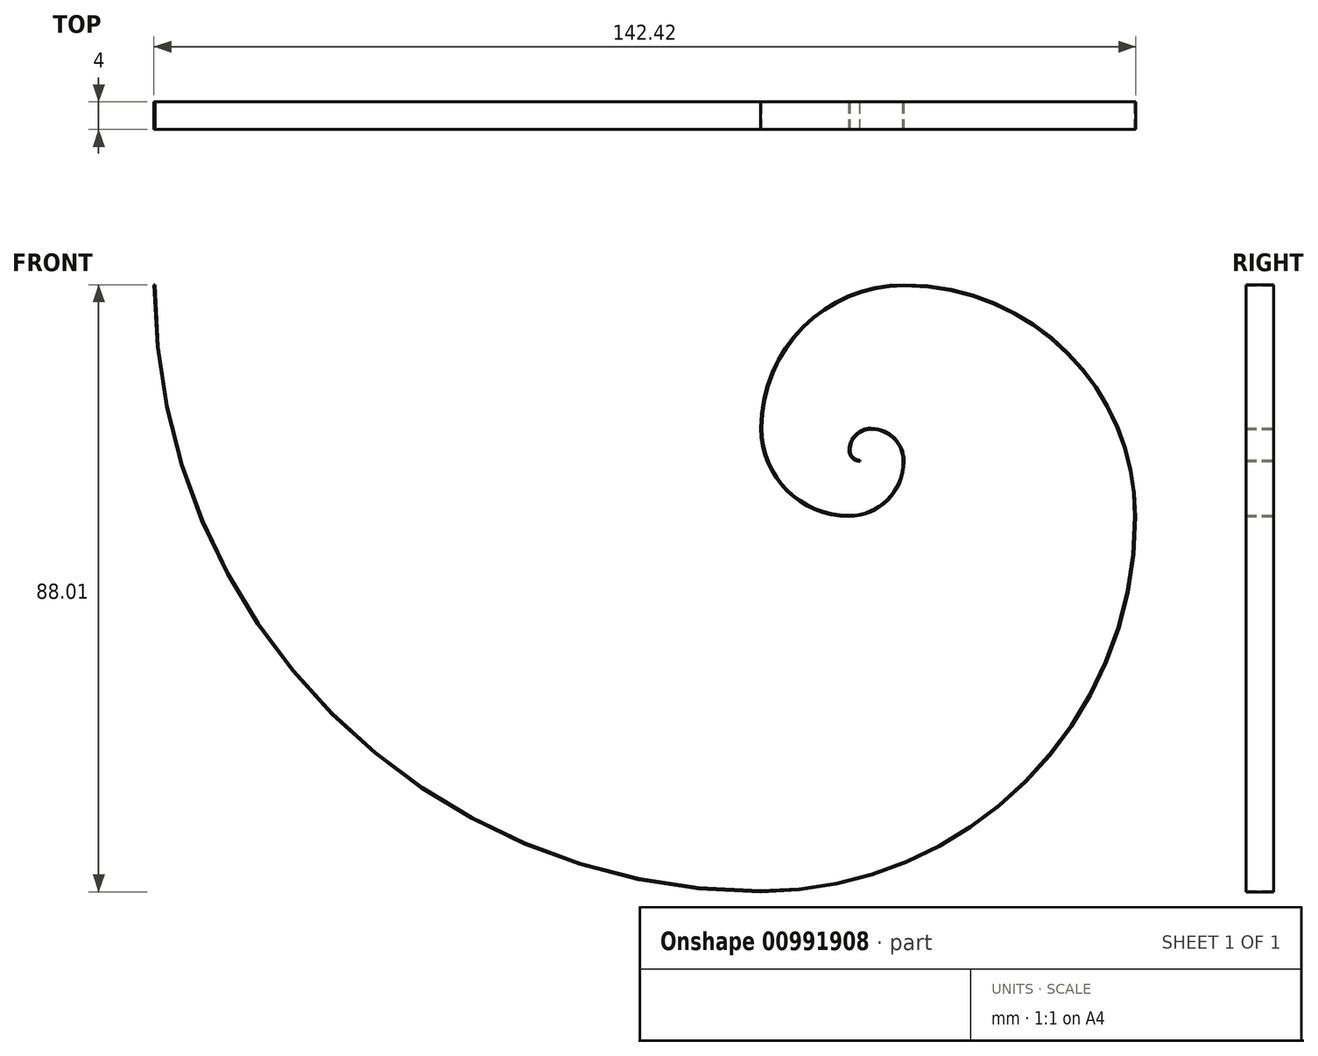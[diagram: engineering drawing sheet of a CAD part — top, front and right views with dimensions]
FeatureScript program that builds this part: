
annotation { "Feature Type Name" : "Feature", "Feature Type Description" : "" }
export const myFeature = defineFeature(function(context is Context, id is Id, definition is map)
    precondition{}
    {
        {
            var Q0;
            Q0=qCreatedBy(makeId("Front.planeOp"),FACE);
            var sketch = newSketch(context, id + "F0", { "sketchPlane" : qUnion([Q0])});
            skLineSegment(sketch, "E0.left", {"start": v(12.7, -12.7) * mm, "end": v(12.7, -10.02) * mm});
            skPoint(sketch, "E0.middle", {"position": v(0, 0) * mm});
            skArc(sketch, "E1", {"start": v(12.7, -12.7) * mm, "mid": v(-5.26, -5.26) * mm, "end": v(-12.7, 12.7) * mm});
            skArc(sketch, "E2", {"start": v(-12.7, 12.7) * mm, "mid": v(2.18, 48.62) * mm, "end": v(38.1, 63.5) * mm});
            skArc(sketch, "E3", {"start": v(38.1, 63.5) * mm, "mid": v(91.98, 41.18) * mm, "end": v(114.3, -12.7) * mm});
            skArc(sketch, "E4", {"start": v(114.3, -12.7) * mm, "mid": v(77.1, -102.5) * mm, "end": v(-12.7, -139.7) * mm});
            skArc(sketch, "E5", {"start": v(-12.7, -139.7) * mm, "mid": v(-156.38, -80.18) * mm, "end": v(-215.9, 63.5) * mm});
            skLineSegment(sketch, "E6.bottom", {"start": v(-1610.22, 393.7) * mm, "end": v(-1612.9, 393.7) * mm});
            skArc(sketch, "E7", {"start": v(-215.9, 63.5) * mm, "mid": v(-119.19, 296.99) * mm, "end": v(114.3, 393.7) * mm});
            skArc(sketch, "E8", {"start": v(114.3, 393.7) * mm, "mid": v(491.47, 237.47) * mm, "end": v(647.7, -139.7) * mm});
            skArc(sketch, "E9", {"start": v(647.7, -139.7) * mm, "mid": v(394.76, -750.36) * mm, "end": v(-215.9, -1003.3) * mm});
            skArc(sketch, "E10", {"start": v(-215.9, -1003.3) * mm, "mid": v(-1203.73, -594.13) * mm, "end": v(-1612.9, 393.7) * mm});
            skArc(sketch, "E11", {"start": v(12.7, -10.02) * mm, "mid": v(-3.37, -3.37) * mm, "end": v(-10.02, 12.7) * mm});
            skArc(sketch, "E12", {"start": v(-10.02, 12.7) * mm, "mid": v(4.07, 46.73) * mm, "end": v(38.1, 60.82) * mm});
            skArc(sketch, "E13", {"start": v(38.1, 60.82) * mm, "mid": v(90.09, 39.29) * mm, "end": v(111.62, -12.7) * mm});
            skArc(sketch, "E14", {"start": v(111.62, -12.7) * mm, "mid": v(75.2, -100.6) * mm, "end": v(-12.7, -137.02) * mm});
            skArc(sketch, "E15", {"start": v(-12.7, -137.02) * mm, "mid": v(-154.5, -78.3) * mm, "end": v(-213.22, 63.5) * mm});
            skArc(sketch, "E16", {"start": v(-213.22, 63.5) * mm, "mid": v(-117.3, 295.1) * mm, "end": v(114.3, 391.02) * mm});
            skArc(sketch, "E17", {"start": v(114.3, 391.02) * mm, "mid": v(489.58, 235.58) * mm, "end": v(645.02, -139.7) * mm});
            skArc(sketch, "E18", {"start": v(645.02, -139.7) * mm, "mid": v(392.86, -748.46) * mm, "end": v(-215.9, -1000.62) * mm});
            skArc(sketch, "E19", {"start": v(-215.9, -1000.62) * mm, "mid": v(-1201.84, -592.24) * mm, "end": v(-1610.22, 393.7) * mm});
            skSolve(sketch);
        }
        {
            var Q0;
            Q0=makeQuery(id+"F0.imprint","IMPRINT",FACE,{"disambiguationData":[TD([[makeQuery(id+"F0.imprint","IMPRINT",EDGE,{"derivedFrom":sQuery(id+"F0.wireOp",EDGE,"E0.left")}),1.0]])]});
            extrude(context, id + "F1", {"entities" : qUnion([Q0]), "depth" : 63.5 * mm, "offsetDistance" : 25.4 * mm});
        }
        {
            var Q0;
            Q0=makeQuery(id+"F1.opExtrude","SWEPT_BODY",BODY,{"disambiguationData":[OSD([sQuery(id+"F0.wireOp",EDGE,"E0.left"),sQuery(id+"F0.wireOp",EDGE,"E1"),sQuery(id+"F0.wireOp",EDGE,"E2"),sQuery(id+"F0.wireOp",EDGE,"E3"),sQuery(id+"F0.wireOp",EDGE,"E4"),sQuery(id+"F0.wireOp",EDGE,"E5"),sQuery(id+"F0.wireOp",EDGE,"E6.bottom"),sQuery(id+"F0.wireOp",EDGE,"E7"),sQuery(id+"F0.wireOp",EDGE,"E8"),sQuery(id+"F0.wireOp",EDGE,"E9"),sQuery(id+"F0.wireOp",EDGE,"E10"),sQuery(id+"F0.wireOp",EDGE,"E11"),sQuery(id+"F0.wireOp",EDGE,"E12"),sQuery(id+"F0.wireOp",EDGE,"E13"),sQuery(id+"F0.wireOp",EDGE,"E14"),sQuery(id+"F0.wireOp",EDGE,"E15"),sQuery(id+"F0.wireOp",EDGE,"E16"),sQuery(id+"F0.wireOp",EDGE,"E17"),sQuery(id+"F0.wireOp",EDGE,"E18"),sQuery(id+"F0.wireOp",EDGE,"E19")])]});
            var Q1;
            Q1=qCreatedBy(makeId("Origin.pointOp"),VERTEX);
            transform(context, id + "F2", {"entities" : qUnion([Q0]), "transformType" : TransformType.SCALE_UNIFORMLY, "scale" : .2, "scalePoint" : qUnion([Q1]), "makeCopy" : false});
        }
        {
            var Q0;
            Q0=makeQuery(id+"F1.opExtrude","SWEPT_BODY",BODY,{"disambiguationData":[OSD([sQuery(id+"F0.wireOp",EDGE,"E0.left"),sQuery(id+"F0.wireOp",EDGE,"E1"),sQuery(id+"F0.wireOp",EDGE,"E2"),sQuery(id+"F0.wireOp",EDGE,"E3"),sQuery(id+"F0.wireOp",EDGE,"E4"),sQuery(id+"F0.wireOp",EDGE,"E5"),sQuery(id+"F0.wireOp",EDGE,"E6.bottom"),sQuery(id+"F0.wireOp",EDGE,"E7"),sQuery(id+"F0.wireOp",EDGE,"E8"),sQuery(id+"F0.wireOp",EDGE,"E9"),sQuery(id+"F0.wireOp",EDGE,"E10"),sQuery(id+"F0.wireOp",EDGE,"E11"),sQuery(id+"F0.wireOp",EDGE,"E12"),sQuery(id+"F0.wireOp",EDGE,"E13"),sQuery(id+"F0.wireOp",EDGE,"E14"),sQuery(id+"F0.wireOp",EDGE,"E15"),sQuery(id+"F0.wireOp",EDGE,"E16"),sQuery(id+"F0.wireOp",EDGE,"E17"),sQuery(id+"F0.wireOp",EDGE,"E18"),sQuery(id+"F0.wireOp",EDGE,"E19")])]});
            var Q1;
            Q1=makeQuery(id+"F1.opExtrude","CAP_VERTEX",VERTEX,{"disambiguationData":[OSD([sQuery(id+"F0.wireOp",EDGE,"E3"),sQuery(id+"F0.wireOp",EDGE,"E4")])],"isStart":false});
            transform(context, id + "F3", {"entities" : qUnion([Q0]), "transformType" : TransformType.SCALE_UNIFORMLY, "scale" : .35, "scalePoint" : qUnion([Q1]), "makeCopy" : false});
        }
        {
            var Q0;
            Q0=makeQuery(id+"F1.opExtrude","SWEPT_BODY",BODY,{"disambiguationData":[OSD([sQuery(id+"F0.wireOp",EDGE,"E0.left"),sQuery(id+"F0.wireOp",EDGE,"E1"),sQuery(id+"F0.wireOp",EDGE,"E2"),sQuery(id+"F0.wireOp",EDGE,"E3"),sQuery(id+"F0.wireOp",EDGE,"E4"),sQuery(id+"F0.wireOp",EDGE,"E5"),sQuery(id+"F0.wireOp",EDGE,"E6.bottom"),sQuery(id+"F0.wireOp",EDGE,"E7"),sQuery(id+"F0.wireOp",EDGE,"E8"),sQuery(id+"F0.wireOp",EDGE,"E9"),sQuery(id+"F0.wireOp",EDGE,"E10"),sQuery(id+"F0.wireOp",EDGE,"E11"),sQuery(id+"F0.wireOp",EDGE,"E12"),sQuery(id+"F0.wireOp",EDGE,"E13"),sQuery(id+"F0.wireOp",EDGE,"E14"),sQuery(id+"F0.wireOp",EDGE,"E15"),sQuery(id+"F0.wireOp",EDGE,"E16"),sQuery(id+"F0.wireOp",EDGE,"E17"),sQuery(id+"F0.wireOp",EDGE,"E18"),sQuery(id+"F0.wireOp",EDGE,"E19")])]});
            transform(context, id + "F4", {"entities" : qUnion([Q0]), "transformType" : TransformType.TRANSLATION_3D, "dx" : 17.78 * mm, "dy" : 0 * mm, "dz" : 0 * mm, "makeCopy" : false});
        }
        {
            var Q0;
            Q0=makeQuery(id+"F1.opExtrude","SWEPT_BODY",BODY,{"disambiguationData":[OSD([sQuery(id+"F0.wireOp",EDGE,"E0.left"),sQuery(id+"F0.wireOp",EDGE,"E1"),sQuery(id+"F0.wireOp",EDGE,"E2"),sQuery(id+"F0.wireOp",EDGE,"E3"),sQuery(id+"F0.wireOp",EDGE,"E4"),sQuery(id+"F0.wireOp",EDGE,"E5"),sQuery(id+"F0.wireOp",EDGE,"E6.bottom"),sQuery(id+"F0.wireOp",EDGE,"E7"),sQuery(id+"F0.wireOp",EDGE,"E8"),sQuery(id+"F0.wireOp",EDGE,"E9"),sQuery(id+"F0.wireOp",EDGE,"E10"),sQuery(id+"F0.wireOp",EDGE,"E11"),sQuery(id+"F0.wireOp",EDGE,"E12"),sQuery(id+"F0.wireOp",EDGE,"E13"),sQuery(id+"F0.wireOp",EDGE,"E14"),sQuery(id+"F0.wireOp",EDGE,"E15"),sQuery(id+"F0.wireOp",EDGE,"E16"),sQuery(id+"F0.wireOp",EDGE,"E17"),sQuery(id+"F0.wireOp",EDGE,"E18"),sQuery(id+"F0.wireOp",EDGE,"E19")])]});
            var Q1;
            Q1=qCreatedBy(makeId("Origin.pointOp"),VERTEX);
            transform(context, id + "F5", {"entities" : qUnion([Q0]), "transformType" : TransformType.SCALE_UNIFORMLY, "scale" : 0.9, "scalePoint" : qUnion([Q1]), "makeCopy" : false});
        }
    });
